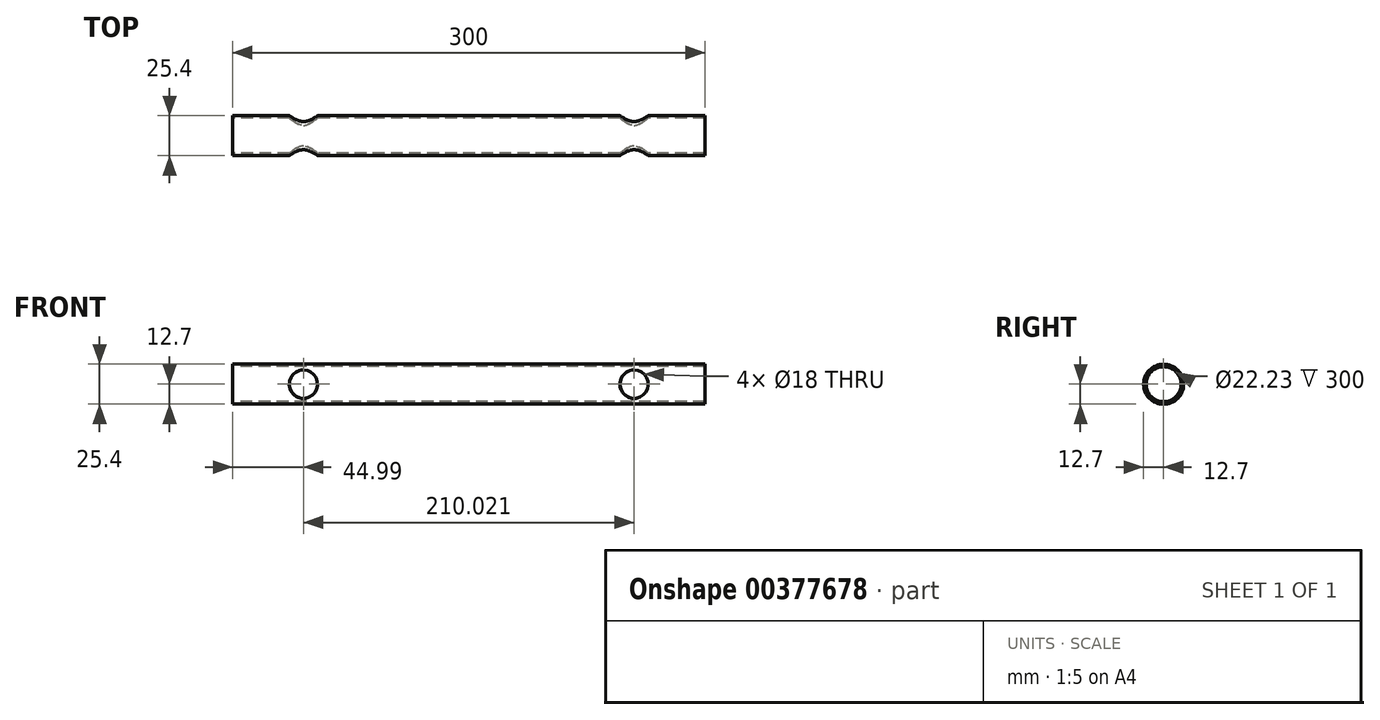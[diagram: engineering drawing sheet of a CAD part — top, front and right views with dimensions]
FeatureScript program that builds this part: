
annotation { "Feature Type Name" : "Feature", "Feature Type Description" : "" }
export const myFeature = defineFeature(function(context is Context, id is Id, definition is map)
    precondition{}
    {
        {
            var Q0;
            Q0=qCreatedBy(makeId("Right.planeOp"),FACE);
            var sketch = newSketch(context, id + "F0", { "sketchPlane" : qUnion([Q0])});
            skCircle(sketch, "E0", {"center": v(0, 0) * mm, "radius": 11.11 * mm});
            skCircle(sketch, "E1", {"center": v(0, 0) * mm, "radius": 12.7 * mm});
            skSolve(sketch);
        }
        {
            var Q0;
            Q0=qSketchRegion(id+"F0",true);
            extrude(context, id + "F1", {"entities" : qUnion([Q0]), "depth" : 300 * mm, "symmetric" : true});
        }
        {
            var Q0;
            Q0=qCreatedBy(makeId("Front.planeOp"),FACE);
            var sketch = newSketch(context, id + "F2", { "sketchPlane" : qUnion([Q0])});
            skLineSegment(sketch, "E2", {"start": v(-142.5, 0) * mm, "end": v(142.9, 0) * mm, "construction": true});
            skCircle(sketch, "E3", {"center": v(-105.01, 0) * mm, "radius": 9 * mm});
            skLineSegment(sketch, "E4", {"start": v(0, 0) * mm, "end": v(0, 28.42) * mm, "construction": true});
            skCircle(sketch, "E5.MirrorC", {"center": v(105.01, 0) * mm, "radius": 9 * mm});
            skSolve(sketch);
        }
        {
            var Q0;
            Q0=qSketchRegion(id+"F2",true);
            extrude(context, id + "F3", {"entities" : qUnion([Q0]), "operationType" : NewBodyOperationType.REMOVE, "depth" : 30 * mm, "symmetric" : true});
        }
    });
